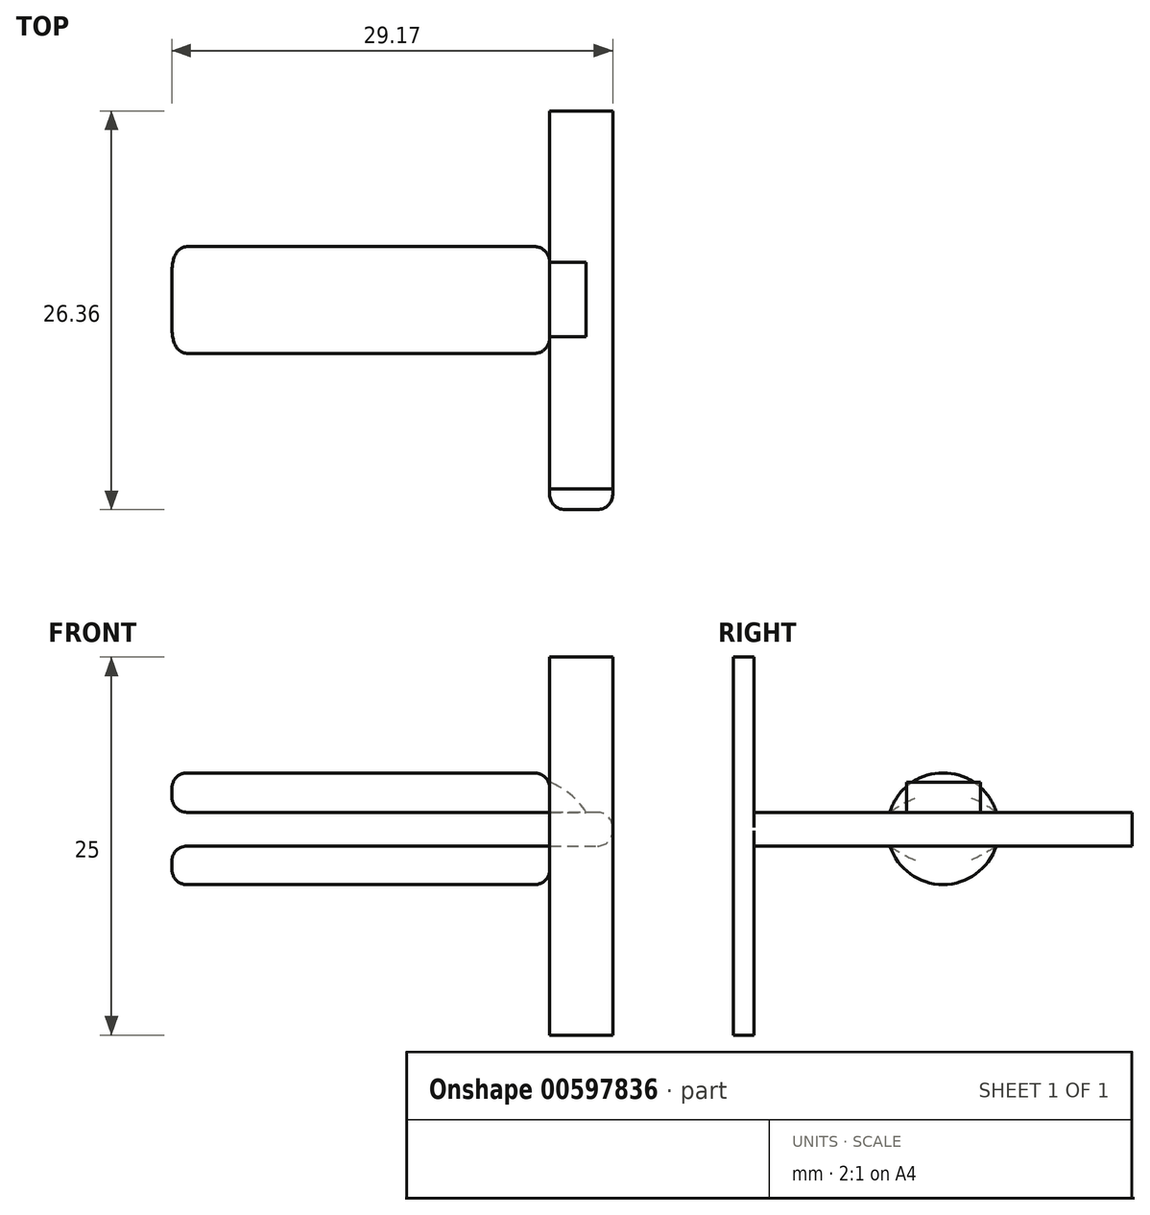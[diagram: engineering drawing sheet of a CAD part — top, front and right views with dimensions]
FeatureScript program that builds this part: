
annotation { "Feature Type Name" : "Feature", "Feature Type Description" : "" }
export const myFeature = defineFeature(function(context is Context, id is Id, definition is map)
    precondition{}
    {
        {
            var Q0;
            Q0=qCreatedBy(makeId("Top.planeOp"),FACE);
            var sketch = newSketch(context, id + "F0", { "sketchPlane" : qUnion([Q0])});
            skLineSegment(sketch, "E0", {"start": v(0, 0) * mm, "end": v(-4.17, 0) * mm});
            skLineSegment(sketch, "E1", {"start": v(-4.17, 0) * mm, "end": v(-4.17, 1.36) * mm});
            skLineSegment(sketch, "E2", {"start": v(-4.17, 1.36) * mm, "end": v(0, 1.36) * mm});
            skLineSegment(sketch, "E3", {"start": v(0, 1.36) * mm, "end": v(0, 0) * mm});
            skSolve(sketch);
        }
        {
            var Q0;
            Q0=makeQuery(id+"F0.imprint","IMPRINT",FACE,{"disambiguationData":[TD([[makeQuery(id+"F0.imprint","IMPRINT",EDGE,{"derivedFrom":sQuery(id+"F0.wireOp",EDGE,"E0")}),-1.0]])]});
            extrude(context, id + "F1", {"entities" : qUnion([Q0]), "depth" : 25 * mm, "offsetDistance" : 25 * mm});
        }
        {
            var Q0;
            Q0=makeQuery(id+"F1.opExtrude","SWEPT_FACE",FACE,{"disambiguationData":[OSD([sQuery(id+"F0.wireOp",EDGE,"E2")])]});
            var sketch = newSketch(context, id + "F2", { "sketchPlane" : qUnion([Q0])});
            skLineSegment(sketch, "E4", {"start": v(4.17, 12.5) * mm, "end": v(0, 12.5) * mm});
            skLineSegment(sketch, "E5", {"start": v(0, 12.5) * mm, "end": v(0, 14.73) * mm});
            skLineSegment(sketch, "E6", {"start": v(0, 14.73) * mm, "end": v(4.17, 14.73) * mm});
            skLineSegment(sketch, "E7", {"start": v(4.17, 14.73) * mm, "end": v(4.17, 12.5) * mm});
            skSolve(sketch);
        }
        {
            var Q0;
            Q0=makeQuery(id+"F2.imprint","IMPRINT",FACE,{"disambiguationData":[TD([[makeQuery(id+"F2.imprint","IMPRINT",EDGE,{"derivedFrom":sQuery(id+"F2.wireOp",EDGE,"E4")}),-1.0]])]});
            extrude(context, id + "F3", {"entities" : qUnion([Q0]), "operationType" : NewBodyOperationType.ADD, "depth" : 25 * mm, "offsetDistance" : 25 * mm});
        }
        {
            var Q0;
            Q0=makeQuery(id+"F3.boolean.opBoolean","MERGE",FACE,{"derivedFrom":[makeQuery(id+"F1.opExtrude","SWEPT_FACE",FACE,{"disambiguationData":[OSD([sQuery(id+"F0.wireOp",EDGE,"E1")])]}),makeQuery(id+"F3.opExtrude","SWEPT_FACE",FACE,{"disambiguationData":[OSD([sQuery(id+"F2.wireOp",EDGE,"E7")])]})]});
            var sketch = newSketch(context, id + "F4", { "sketchPlane" : qUnion([Q0])});
            skCircle(sketch, "E8", {"center": v(-13.86, 13.64) * mm, "radius": 3.7 * mm});
            skPoint(sketch, "E8.centerSnap0", {"position": v(-13.86, 12.5) * mm});
            skSolve(sketch);
        }
        {
            var Q0;
            {var subQ0=sQuery(id+"F4.wireOp",EDGE,"E8");var subQ1=makeQuery(id+"F3.opExtrude","SWEPT_EDGE",EDGE,{"disambiguationData":[OSD([sQuery(id+"F0.wireOp",EDGE,"E1"),sQuery(id+"F0.wireOp",EDGE,"E2"),sQuery(id+"F2.wireOp",EDGE,"E6"),sQuery(id+"F2.wireOp",EDGE,"E7")])]});var subQ2=makeQuery(id+"F4.imprint","INTERSECT",VERTEX,{"disambiguationData":[OD(0.0)],"derivedFrom":[subQ1,subQ0]});Q0=makeQuery(id+"F4.imprint","IMPRINT",FACE,{"disambiguationData":[TD([[makeQuery(id+"F4.imprint","IMPRINT",EDGE,{"disambiguationData":[TD([[subQ2,1.0]])],"derivedFrom":subQ0}),1.0]])]});}
            var Q1;
            {var subQ0=sQuery(id+"F4.wireOp",EDGE,"E8");var subQ1=makeQuery(id+"F3.opExtrude","SWEPT_EDGE",EDGE,{"disambiguationData":[OSD([sQuery(id+"F0.wireOp",EDGE,"E1"),sQuery(id+"F0.wireOp",EDGE,"E2"),sQuery(id+"F2.wireOp",EDGE,"E4"),sQuery(id+"F2.wireOp",EDGE,"E7")])]});var subQ2=makeQuery(id+"F4.imprint","INTERSECT",VERTEX,{"disambiguationData":[OD(0.0)],"derivedFrom":[subQ1,subQ0]});Q1=makeQuery(id+"F4.imprint","IMPRINT",FACE,{"disambiguationData":[TD([[makeQuery(id+"F4.imprint","IMPRINT",EDGE,{"disambiguationData":[TD([[subQ2,-1.0]])],"derivedFrom":subQ0}),1.0]])]});}
            extrude(context, id + "F5", {"entities" : qUnion([Q0, Q1]), "depth" : 25 * mm, "offsetDistance" : 25 * mm});
        }
        {
            var Q0;
            {var subQ0=sQuery(id+"F4.wireOp",EDGE,"E8");var subQ1=makeQuery(id+"F3.opExtrude","SWEPT_EDGE",EDGE,{"disambiguationData":[OSD([sQuery(id+"F0.wireOp",EDGE,"E1"),sQuery(id+"F0.wireOp",EDGE,"E2"),sQuery(id+"F2.wireOp",EDGE,"E6"),sQuery(id+"F2.wireOp",EDGE,"E7")])]});Q0=makeQuery(id+"F5.opExtrude","CAP_EDGE",EDGE,{"disambiguationData":[OSD([subQ0]),TDD([makeQuery(id+"F4.imprint","IMPRINT",EDGE,{"disambiguationData":[TD([[makeQuery(id+"F4.imprint","INTERSECT",VERTEX,{"disambiguationData":[OD(0.0)],"derivedFrom":[subQ1,subQ0]}),1.0]])],"derivedFrom":subQ0})])],"isStart":true});}
            var Q1;
            {var subQ0=sQuery(id+"F4.wireOp",EDGE,"E8");var subQ1=makeQuery(id+"F3.opExtrude","SWEPT_EDGE",EDGE,{"disambiguationData":[OSD([sQuery(id+"F0.wireOp",EDGE,"E1"),sQuery(id+"F0.wireOp",EDGE,"E2"),sQuery(id+"F2.wireOp",EDGE,"E4"),sQuery(id+"F2.wireOp",EDGE,"E7")])]});Q1=makeQuery(id+"F5.opExtrude","CAP_EDGE",EDGE,{"disambiguationData":[OSD([subQ0]),TDD([makeQuery(id+"F4.imprint","IMPRINT",EDGE,{"disambiguationData":[TD([[makeQuery(id+"F4.imprint","INTERSECT",VERTEX,{"disambiguationData":[OD(0.0)],"derivedFrom":[subQ1,subQ0]}),-1.0]])],"derivedFrom":subQ0})])],"isStart":true});}
            var Q2;
            {var subQ0=sQuery(id+"F4.wireOp",EDGE,"E8");var subQ1=makeQuery(id+"F3.opExtrude","SWEPT_EDGE",EDGE,{"disambiguationData":[OSD([sQuery(id+"F0.wireOp",EDGE,"E1"),sQuery(id+"F0.wireOp",EDGE,"E2"),sQuery(id+"F2.wireOp",EDGE,"E4"),sQuery(id+"F2.wireOp",EDGE,"E7")])]});Q2=makeQuery(id+"F5.opExtrude","CAP_EDGE",EDGE,{"disambiguationData":[OSD([subQ0]),TDD([makeQuery(id+"F4.imprint","IMPRINT",EDGE,{"disambiguationData":[TD([[makeQuery(id+"F4.imprint","INTERSECT",VERTEX,{"disambiguationData":[OD(0.0)],"derivedFrom":[subQ1,subQ0]}),-1.0]])],"derivedFrom":subQ0})])],"isStart":false});}
            var Q3;
            Q3=makeQuery(id+"F5.opExtrude","CAP_EDGE",EDGE,{"disambiguationData":[OSD([sQuery(id+"F0.wireOp",EDGE,"E1"),sQuery(id+"F0.wireOp",EDGE,"E2"),sQuery(id+"F2.wireOp",EDGE,"E4"),sQuery(id+"F2.wireOp",EDGE,"E7")])],"isStart":false});
            var Q4;
            Q4=makeQuery(id+"F5.opExtrude","CAP_EDGE",EDGE,{"disambiguationData":[OSD([sQuery(id+"F0.wireOp",EDGE,"E1"),sQuery(id+"F0.wireOp",EDGE,"E2"),sQuery(id+"F2.wireOp",EDGE,"E6"),sQuery(id+"F2.wireOp",EDGE,"E7")])],"isStart":false});
            var Q5;
            {var subQ0=sQuery(id+"F4.wireOp",EDGE,"E8");var subQ1=makeQuery(id+"F3.opExtrude","SWEPT_EDGE",EDGE,{"disambiguationData":[OSD([sQuery(id+"F0.wireOp",EDGE,"E1"),sQuery(id+"F0.wireOp",EDGE,"E2"),sQuery(id+"F2.wireOp",EDGE,"E6"),sQuery(id+"F2.wireOp",EDGE,"E7")])]});Q5=makeQuery(id+"F5.opExtrude","CAP_EDGE",EDGE,{"disambiguationData":[OSD([subQ0]),TDD([makeQuery(id+"F4.imprint","IMPRINT",EDGE,{"disambiguationData":[TD([[makeQuery(id+"F4.imprint","INTERSECT",VERTEX,{"disambiguationData":[OD(0.0)],"derivedFrom":[subQ1,subQ0]}),1.0]])],"derivedFrom":subQ0})])],"isStart":false});}
            var Q6;
            Q6=makeQuery(id+"F1.opExtrude","SWEPT_EDGE",EDGE,{"disambiguationData":[OSD([sQuery(id+"F0.wireOp",EDGE,"E0"),sQuery(id+"F0.wireOp",EDGE,"E1")])]});
            var Q7;
            Q7=makeQuery(id+"F1.opExtrude","SWEPT_EDGE",EDGE,{"disambiguationData":[OSD([sQuery(id+"F0.wireOp",EDGE,"E0"),sQuery(id+"F0.wireOp",EDGE,"E3")])]});
            var Q8;
            Q8=makeQuery(id+"F3.opExtrude","SWEPT_EDGE",EDGE,{"disambiguationData":[OSD([sQuery(id+"F0.wireOp",EDGE,"E2"),sQuery(id+"F0.wireOp",EDGE,"E3"),sQuery(id+"F2.wireOp",EDGE,"E5"),sQuery(id+"F2.wireOp",EDGE,"E6")])]});
            var Q9;
            Q9=makeQuery(id+"F3.opExtrude","SWEPT_EDGE",EDGE,{"disambiguationData":[OSD([sQuery(id+"F0.wireOp",EDGE,"E2"),sQuery(id+"F0.wireOp",EDGE,"E3"),sQuery(id+"F2.wireOp",EDGE,"E4"),sQuery(id+"F2.wireOp",EDGE,"E5")])]});
            fillet(context, id + "F6", {"entities" : qUnion([Q0, Q1, Q2, Q3, Q4, Q5, Q6, Q7, Q8, Q9]), "radius" : 1 * mm, "tangentPropagation" : true, "allowEdgeOverflow" : false});
        }
        {
            var Q0;
            Q0=makeQuery(id+"F3.opExtrude","SWEPT_FACE",FACE,{"disambiguationData":[OSD([sQuery(id+"F2.wireOp",EDGE,"E6")])]});
            var sketch = newSketch(context, id + "F7", { "sketchPlane" : qUnion([Q0])});
            skLineSegment(sketch, "E9", {"start": v(-4.17, 16.34) * mm, "end": v(-4.17, 11.45) * mm});
            skLineSegment(sketch, "E10", {"start": v(-4.17, 11.45) * mm, "end": v(-1, 11.45) * mm});
            skLineSegment(sketch, "E11", {"start": v(-1, 11.45) * mm, "end": v(-1, 16.34) * mm});
            skLineSegment(sketch, "E12", {"start": v(-1, 16.34) * mm, "end": v(-4.17, 16.34) * mm});
            skSolve(sketch);
        }
        {
            var Q0;
            Q0=makeQuery(id+"F7.imprint","IMPRINT",FACE,{"disambiguationData":[TD([[makeQuery(id+"F7.imprint","IMPRINT",EDGE,{"derivedFrom":sQuery(id+"F7.wireOp",EDGE,"E9")}),1.0]])]});
            extrude(context, id + "F8", {"entities" : qUnion([Q0]), "depth" : 2 * mm, "offsetDistance" : 25 * mm});
        }
        {
            var Q0;
            Q0=makeQuery(id+"F8.opExtrude","CAP_EDGE",EDGE,{"disambiguationData":[OSD([sQuery(id+"F7.wireOp",EDGE,"E11")])],"isStart":false});
            fillet(context, id + "F9", {"entities" : qUnion([Q0]), "radius" : 5 * mm, "tangentPropagation" : true, "allowEdgeOverflow" : false});
        }
    });
